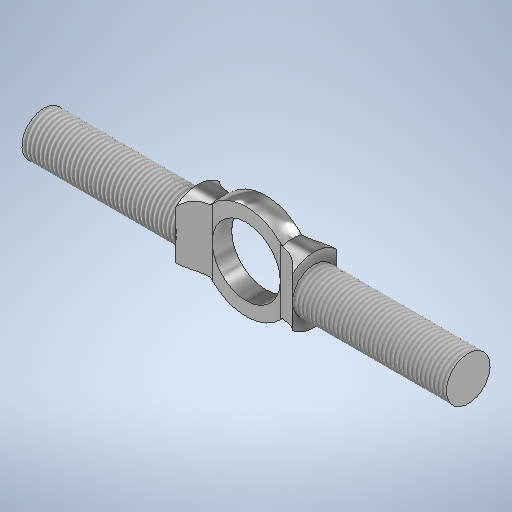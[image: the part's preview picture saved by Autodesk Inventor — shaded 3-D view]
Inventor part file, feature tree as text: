
AUTODESK INVENTOR PART (.ipt)
format: ipt  version: 2025.2 (Build 292293000, 293)  size: 347,136 bytes
history: native  units: in
note: dims shown in document units (in); Inventor stores cm internally (conversion verified against a paired STEP export)
features: other x3, extrude x2, thread x2, revolve x1
ambient origin geometry x8: Origin, YZ Plane, XZ Plane, XY Plane, X Axis, Y Axis, Z Axis, Center Point
bodies: Volumenkörper1 (feature_tree)
feature tree (8):
  other  "Skelett_Laufkatze.ipt"
  revolve  "Umdrehung1"
  extrude  "Extrusion1"  Depth=0.3937in
  extrude  "Extrusion2"  TaperAngle=90.0deg  [1 undecoded]
  thread  "Gewinde1"  [1 undecoded]
  thread  "Gewinde2"  [1 undecoded]
  other  "Schraubbolzen_oben"
  other  "Schraubbolzen_Ankerausschnitt"
note: 3 required parameter values undecoded (feature->parameter linkage not recoverable at this tier; creation-order binding heuristic only, values carry confidence <= 0.55)
